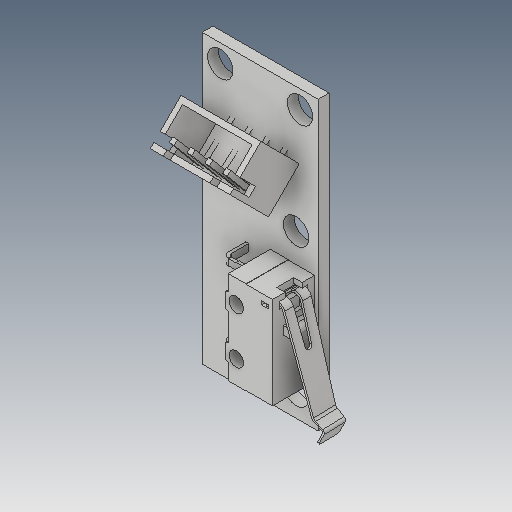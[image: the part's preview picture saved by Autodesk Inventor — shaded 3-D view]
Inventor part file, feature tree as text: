
AUTODESK INVENTOR PART (.ipt)
format: ipt  version: 2017 (Build 210142000, 142)  size: 382,464 bytes
history: native  units: mm
features: other x12, revolve x2, direct_edit x1, move_body x1
ambient origin geometry x8: Origin, YZ Plane, XZ Plane, XY Plane, X Axis, Y Axis, Z Axis, Center Point
bodies: Solid1 (feature_tree), Solid2 (feature_tree), Solid3 (feature_tree), Solid4 (feature_tree), Solid5 (feature_tree), Solid6 (feature_tree), Solid7 (feature_tree), Solid8 (feature_tree), Solid9 (feature_tree), Solid10 (feature_tree), Solid11 (feature_tree), Solid12 (feature_tree)
feature tree (16):
  direct_edit  "Direct Edit1"
  other  "Embase alim end stop.1:1"
  other  "Embase alim end stop.1:2"
  other  "Embase alim end stop.1:3"
  other  "Embase alim end stop.1:4"
  other  "Embase alim end stop.1:5"
  other  "Boitier plastique:1"
  other  "Bouton:1"
  other  "Levier:1"
  other  "Contact:1"
  other  "Contact 2:1"
  other  "Contact 3:1"
  other  "Pièce1.1:1"
  revolve  "Rotate1"  Angle=45.0deg
  move_body  "Move1"
  revolve  "Rotate2"  [1 undecoded]
note: 1 required parameter value undecoded (feature->parameter linkage not recoverable at this tier; creation-order binding heuristic only, values carry confidence <= 0.55)
